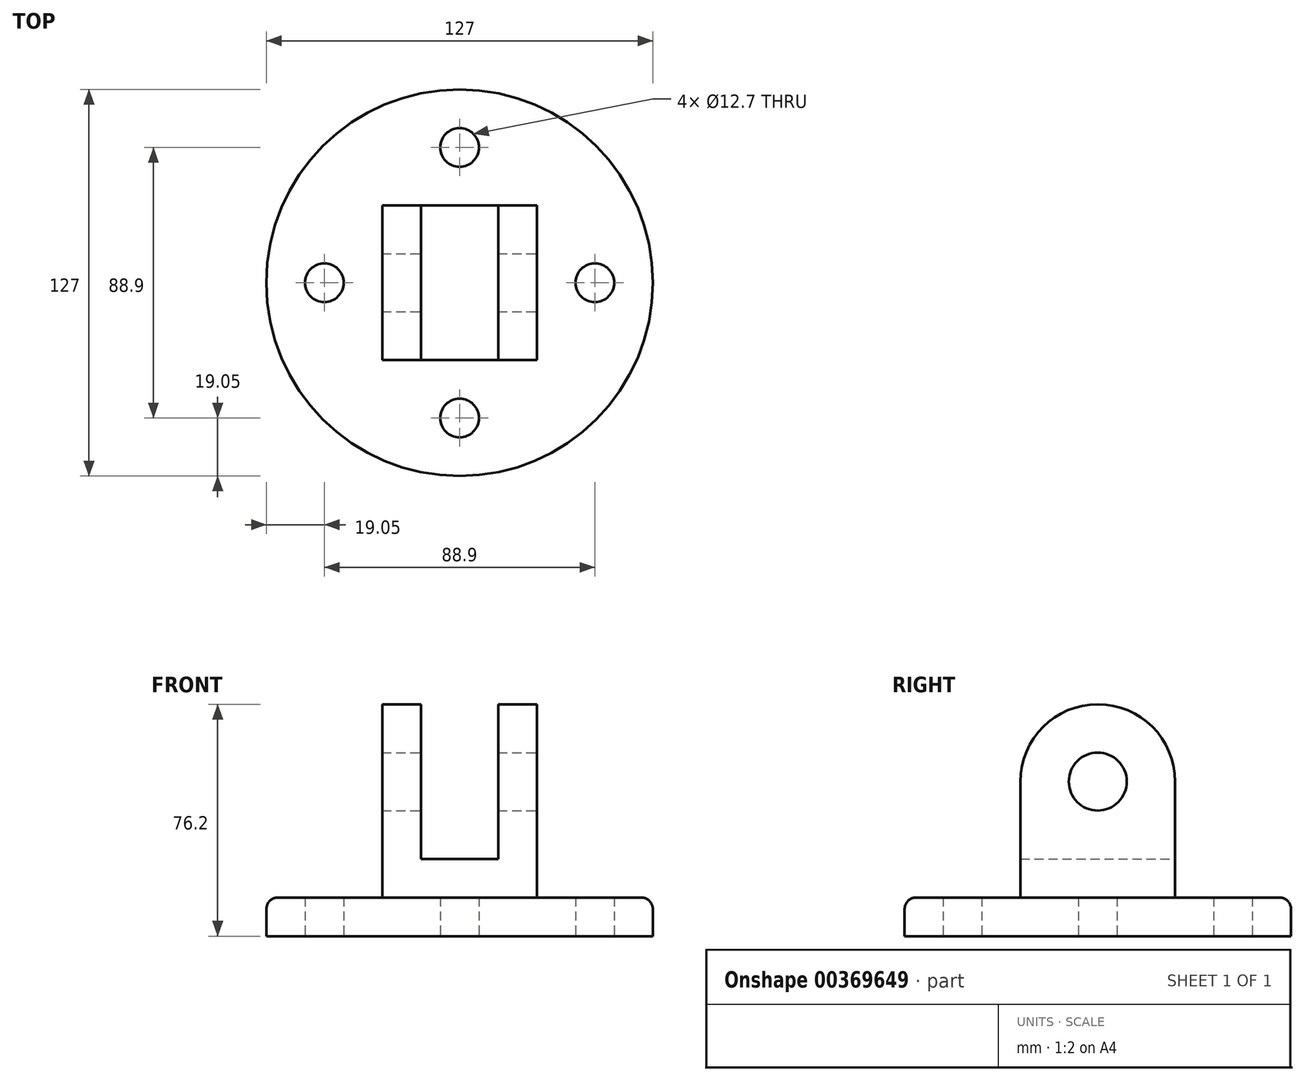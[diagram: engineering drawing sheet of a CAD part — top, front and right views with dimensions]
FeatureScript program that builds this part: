
annotation { "Feature Type Name" : "Feature", "Feature Type Description" : "" }
export const myFeature = defineFeature(function(context is Context, id is Id, definition is map)
    precondition{}
    {
        {
            var Q0;
            Q0=qCreatedBy(makeId("Top.planeOp"),FACE);
            var sketch = newSketch(context, id + "F0", { "sketchPlane" : qUnion([Q0])});
            skCircle(sketch, "E0", {"center": v(0, 0) * mm, "radius": 63.5 * mm});
            skCircle(sketch, "E1", {"center": v(0, 44.45) * mm, "radius": 6.35 * mm});
            skCircle(sketch, "E2.1.0", {"center": v(-44.45, 0) * mm, "radius": 6.35 * mm});
            skCircle(sketch, "E2.2.0", {"center": v(0, -44.45) * mm, "radius": 6.35 * mm});
            skCircle(sketch, "E2.3.0", {"center": v(44.45, 0) * mm, "radius": 6.35 * mm});
            skSolve(sketch);
        }
        {
            var Q0;
            Q0 = qSketchRegion(id + "F0", true);
            extrude(context, id + "F1", {"entities" : qUnion([Q0]), "depth" : 12.7 * mm});
        }
        {
            var Q0;
            Q0=qCreatedBy(makeId("Front.planeOp"),FACE);
            var sketch = newSketch(context, id + "F2", { "sketchPlane" : qUnion([Q0])});
            skLineSegment(sketch, "E3", {"start": v(-25.4, 12.7) * mm, "end": v(-25.4, 76.2) * mm});
            skLineSegment(sketch, "E4", {"start": v(-25.4, 76.2) * mm, "end": v(-12.7, 76.2) * mm});
            skLineSegment(sketch, "E5", {"start": v(-12.7, 76.2) * mm, "end": v(-12.7, 25.4) * mm});
            skLineSegment(sketch, "E6", {"start": v(-12.7, 25.4) * mm, "end": v(12.7, 25.4) * mm});
            skLineSegment(sketch, "E7", {"start": v(12.7, 25.4) * mm, "end": v(12.7, 76.2) * mm});
            skLineSegment(sketch, "E8", {"start": v(12.7, 76.2) * mm, "end": v(25.4, 76.2) * mm});
            skLineSegment(sketch, "E9", {"start": v(25.4, 76.2) * mm, "end": v(25.4, 12.7) * mm});
            skLineSegment(sketch, "E10", {"start": v(25.4, 12.7) * mm, "end": v(-25.4, 12.7) * mm});
            skSolve(sketch);
        }
        {
            var Q0;
            Q0 = qSketchRegion(id + "F2", true);
            extrude(context, id + "F3", {"entities" : qUnion([Q0]), "operationType" : NewBodyOperationType.ADD, "endBound" : BoundingType.SYMMETRIC, "depth" : 50.8 * mm});
        }
        {
            var Q0;
            Q0=qCreatedBy(makeId("Right.planeOp"),FACE);
            var sketch = newSketch(context, id + "F4", { "sketchPlane" : qUnion([Q0])});
            skCircle(sketch, "E11", {"center": v(0, 50.8) * mm, "radius": 9.53 * mm});
            skArc(sketch, "E12", {"start": v(25.4, 50.8) * mm, "mid": v(0, 76.2) * mm, "end": v(-25.4, 50.8) * mm});
            skLineSegment(sketch, "E13", {"start": v(-25.4, 50.8) * mm, "end": v(-25.4, 76.2) * mm});
            skLineSegment(sketch, "E14", {"start": v(-25.4, 76.2) * mm, "end": v(25.4, 76.2) * mm});
            skLineSegment(sketch, "E15", {"start": v(25.4, 76.2) * mm, "end": v(25.4, 50.8) * mm});
            skSolve(sketch);
        }
        {
            var Q0;
            Q0 = qSketchRegion(id + "F4", true);
            extrude(context, id + "F5", {"entities" : qUnion([Q0]), "operationType" : NewBodyOperationType.REMOVE, "endBound" : BoundingType.SYMMETRIC, "oppositeDirection" : true, "depth" : 50.8 * mm});
        }
        {
            var Q0;
            Q0=makeQuery(id+"F1.opExtrude","CAP_EDGE",EDGE,{"disambiguationData":[OSD([sQuery(id+"F0.wireOp",EDGE,"E0")])],"isStart":false});
            var Q1;
            Q1=makeQuery(id+"F3.opExtrude","SWEPT_EDGE",EDGE,{"disambiguationData":[OSD([sQuery(id+"F2.wireOp",EDGE,"E9"),sQuery(id+"F2.wireOp",EDGE,"E10")])]});
            var Q2;
            Q2=makeQuery(id+"F3.opExtrude","CAP_EDGE",EDGE,{"disambiguationData":[OSD([sQuery(id+"F2.wireOp",EDGE,"E10")])],"isStart":false});
            var Q3;
            Q3=makeQuery(id+"F3.opExtrude","SWEPT_EDGE",EDGE,{"disambiguationData":[OSD([sQuery(id+"F2.wireOp",EDGE,"E3"),sQuery(id+"F2.wireOp",EDGE,"E10")])]});
            var Q4;
            Q4=makeQuery(id+"F3.opExtrude","CAP_EDGE",EDGE,{"disambiguationData":[OSD([sQuery(id+"F2.wireOp",EDGE,"E10")])],"isStart":true});
            fillet(context, id + "F6", {"entities" : qUnion([Q0, Q1, Q2, Q3, Q4]), "radius" : 3.8 * mm, "tangentPropagation" : true, "allowEdgeOverflow" : false});
        }
    });
